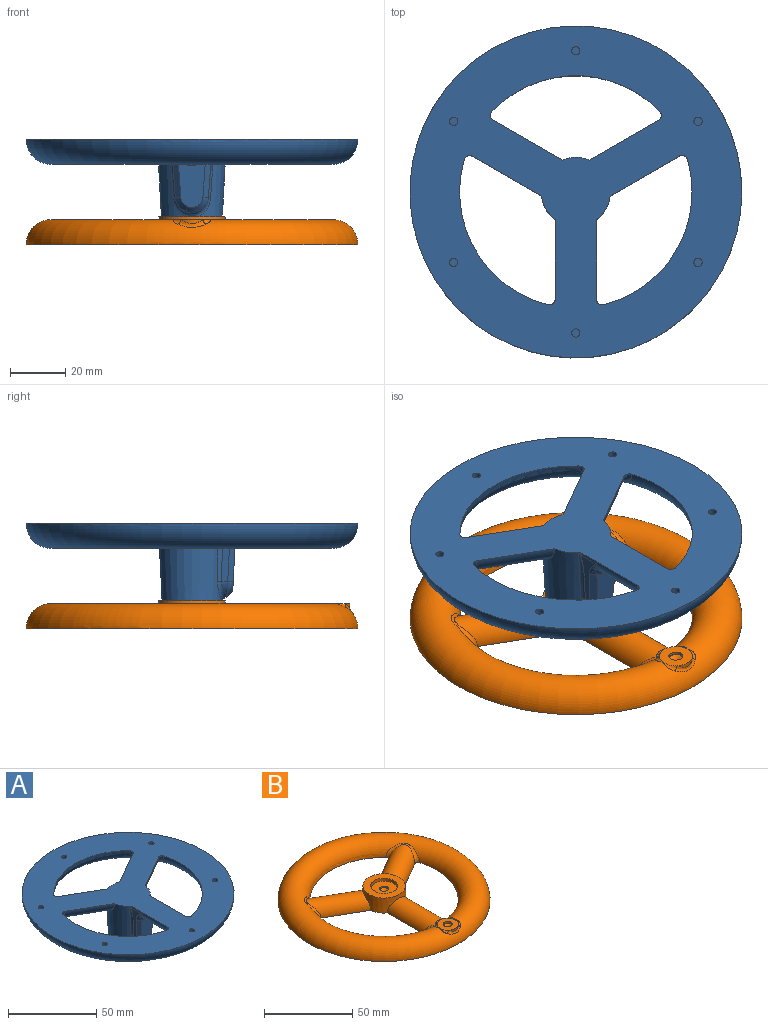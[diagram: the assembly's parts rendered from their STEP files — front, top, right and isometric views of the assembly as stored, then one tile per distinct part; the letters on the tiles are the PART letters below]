
ASSEMBLY  parts=2 mates=1
PART A: 42 faces, bbox 130.1x130.1x36.6 mm
  f0: plane 3x3mm, normal (0,0,1), area 7.1mm2, adj f1
  f1: cylinder r=1.5mm len=5mm, axis (0,0,-1), area 47.1mm2, adj f0,f2
  f2: plane 120.1x120.1mm, normal (0,0,1), area 7578.2mm2, adj f1,f4,f6,f8,f10,f12,f32,f33
  f3: plane 3x3mm, normal (0,0,1), area 7.1mm2, adj f4
  f4: cylinder r=1.5mm len=5mm, axis (0,0,-1), area 47.1mm2, adj f2,f3
  f5: plane 3x3mm, normal (0,0,1), area 7.1mm2, adj f6
  f6: cylinder r=1.5mm len=5mm, axis (0,0,-1), area 47.1mm2, adj f2,f5
  f7: plane 3x3mm, normal (0,0,1), area 7.1mm2, adj f8
  f8: cylinder r=1.5mm len=5mm, axis (0,0,-1), area 47.1mm2, adj f2,f7
  f9: plane 3x3mm, normal (0,0,1), area 7.1mm2, adj f10
  f10: cylinder r=1.5mm len=5mm, axis (0,0,-1), area 47.1mm2, adj f2,f9
  f11: plane 3x3mm, normal (0,0,1), area 7.1mm2, adj f12
  f12: cylinder r=1.5mm len=5mm, axis (0,0,-1), area 47.1mm2, adj f2,f11
  f13: bspline ~7.51x5.63mm, area 15.8mm2, adj f16,f17,f19,f20
  f14: bspline ~5.21x4.56mm, area 15.8mm2, adj f16,f18,f20,f21
  f15: cone r=0mm half-angle=59deg, axis (0,0,-1), area 22.9mm2, adj f22
  f16: plane 16.69x9.85mm, normal (0,-1,-0.05), area 128.1mm2, adj f13,f14,f17,f18,f20,f24
  f17: plane 12.89x2.93mm, normal (-0.7,-0.7,-0.09), area 36.6mm2, adj f13,f16,f25,f26
  f18: plane 12.89x2.93mm, normal (0.7,-0.7,-0.09), area 36.6mm2, adj f14,f16,f23,f27
  f19: cylinder r=6mm len=5.17mm, axis (0,1,0), area 7.3mm2, adj f13,f26,f29
  f20: bspline ~4.29x2.17mm, area 9.8mm2, adj f13,f14,f16,f29
  f21: cylinder r=6mm len=5.17mm, axis (0,1,0), area 7.3mm2, adj f14,f27,f29
  f22: cylinder r=2.5mm len=5mm, axis (0,0,-1), area 15.7mm2, adj f15,f31
  f23: bspline ~7.06x4.35mm, area 13.1mm2, adj f18,f24,f27,f41
  f24: bspline ~18.77x8.24mm, area 48.4mm2, adj f16,f23,f25,f41
  f25: bspline ~7.06x4.35mm, area 13.1mm2, adj f17,f24,f26,f41
  f26: plane 20.08x7.79mm, normal (-1,0,-0.07), area 62.3mm2, adj f17,f19,f25,f28,f33,f41
  f27: plane 20.08x7.79mm, normal (1,0,-0.07), area 62.3mm2, adj f18,f21,f23,f30,f32,f41
  f28: bspline ~21x2.21mm, area 30.7mm2, adj f26,f29,f33,f34
  f29: bspline ~13.63x9.03mm, area 48.7mm2, adj f19,f20,f21,f28,f30,f34
  f30: bspline ~21x2.21mm, area 30.7mm2, adj f27,f29,f32,f34
  f31: plane 21.86x21.86mm, normal (0,0,-1), area 355.5mm2, adj f22,f34
  f32: cone r=12.5mm half-angle=3deg, axis (0,0,-1), area 1.2mm2, adj f2,f27,f30,f41
  f33: cone r=12.5mm half-angle=3deg, axis (0,0,-1), area 3.6mm2, adj f2,f26,f28,f41
  f34: cone r=12.5mm half-angle=3deg, axis (0,0,1), area 1603.5mm2, adj f2,f28,f29,f30,f31,f39,f40
  f35: bspline ~17.28x11.32mm, area 65.2mm2, adj f2,f38,f40
  f36: bspline ~17.28x11.32mm, area 65.2mm2, adj f2,f38,f39
  f37: bspline ~19.97x8.68mm, area 65.2mm2, adj f2,f38,f41
  f38: torus R=51mm, axis (0,0,1), area 8643.7mm2, adj f2,f35,f36,f37
  f39: cylinder r=7.5mm len=38.21mm, axis (-0.87,-0.5,0), area 745.3mm2, adj f2,f34,f36
  f40: cylinder r=7.5mm len=32.49mm, axis (0.87,-0.5,0), area 679.9mm2, adj f2,f34,f35
  f41: cylinder r=7.5mm len=35.46mm, axis (0,1,0), area 588.8mm2, adj f2,f23,f24,f25,f26,f27,f32,f33
PART B: 45 faces, bbox 130x130x16.5 mm
  f0: bspline ~8.05x7.66mm, area 27.6mm2, adj f1,f5,f14,f32
  f1: cylinder r=7.5mm len=34.05mm, axis (0,1,0), area 718.7mm2, adj f0,f6,f15,f17,f19,f20,f32
  f2: cylinder r=6mm len=1.15mm, axis (0,0,-1), area 0.2mm2, adj f9,f12,f17
  f3: cylinder r=7.5mm len=38.23mm, axis (0.87,-0.5,0), area 728.8mm2, adj f6,f24,f32
  f4: cylinder r=7.5mm len=38.23mm, axis (-0.87,-0.5,0), area 728.2mm2, adj f6,f25,f32
  f5: torus R=51mm, axis (0,0,1), area 8497.3mm2, adj f0,f11,f12,f13,f15,f16,f21,f22
  f6: cone r=12.5mm half-angle=3deg, axis (0,0,-1), area 490.2mm2, adj f1,f3,f4,f7,f32
  f7: plane 23.95x23.95mm, normal (0,0,1), area 273.9mm2, adj f6,f26
  f8: cylinder r=6mm len=1.15mm, axis (0,0,-1), area 0.2mm2, adj f9,f16,f20
  f9: plane 12.04x12.04mm, normal (0,0,1), area 93.5mm2, adj f2,f8,f10,f11,f13,f19,f21,f23
  f10: cylinder r=6mm len=7.78mm, axis (0,0,-1), area 7.8mm2, adj f9,f22
  f11: bspline ~5.19x3.19mm, area 6.7mm2, adj f5,f9,f12
  f12: bspline ~2.95x2.6mm, area 1.5mm2, adj f2,f5,f11,f14
  f13: bspline ~5.19x3.19mm, area 6.7mm2, adj f5,f9,f16
  f14: sphere r=2mm, area 2.1mm2, adj f0,f12,f17
  f15: bspline ~7.89x7.23mm, area 27.6mm2, adj f1,f5,f18,f32
  f16: bspline ~2.95x2.6mm, area 1.5mm2, adj f5,f8,f13,f18
  f17: bspline ~3.05x2.9mm, area 2.2mm2, adj f1,f2,f14,f19
  f18: sphere r=2mm, area 2.1mm2, adj f15,f16,f20
  f19: bspline ~5.89x2.75mm, area 12.4mm2, adj f1,f9,f17,f20
  f20: bspline ~2.57x2.5mm, area 2.2mm2, adj f1,f8,f18,f19
  f21: bspline ~5.86x3.51mm, area 6.7mm2, adj f5,f9,f22
  f22: bspline ~11.01x3.2mm, area 17.5mm2, adj f5,f10,f21,f23
  f23: bspline ~5.86x3.51mm, area 6.7mm2, adj f5,f9,f22
  f24: bspline ~17.29x11.33mm, area 65.2mm2, adj f3,f5,f32
  f25: bspline ~17.29x11.33mm, area 65.2mm2, adj f4,f5,f32
  f26: cylinder r=7.5mm len=15mm, axis (0,0,1), area 94.2mm2, adj f7,f27
  f27: plane 15x15mm, normal (0,0,1), area 157.1mm2, adj f26,f31
  f28: cone r=0mm half-angle=59deg, axis (0,0,1), area 22.9mm2, adj f29
  f29: cylinder r=2.5mm len=5mm, axis (0,0,1), area 15.7mm2, adj f9,f28
  f30: cone r=0mm half-angle=59deg, axis (0,0,1), area 22.9mm2, adj f31
  f31: cylinder r=2.5mm len=5mm, axis (0,0,1), area 15.7mm2, adj f27,f30
  f32: plane 120.1x120.1mm, normal (0,0,-1), area 7578.2mm2, adj f0,f1,f3,f4,f5,f6,f15,f24
  f33: cylinder r=1.5mm len=5mm, axis (0,0,-1), area 47.1mm2, adj f32,f34
  f34: plane 3x3mm, normal (0,0,-1), area 7.1mm2, adj f33
  f35: cylinder r=1.5mm len=5mm, axis (0,0,-1), area 47.1mm2, adj f32,f36
  f36: plane 3x3mm, normal (0,0,-1), area 7.1mm2, adj f35
  f37: cylinder r=1.5mm len=5mm, axis (0,0,-1), area 47.1mm2, adj f32,f38
  f38: plane 3x3mm, normal (0,0,-1), area 7.1mm2, adj f37
  f39: cylinder r=1.5mm len=5mm, axis (0,0,-1), area 47.1mm2, adj f32,f40
  f40: plane 3x3mm, normal (0,0,-1), area 7.1mm2, adj f39
  f41: cylinder r=1.5mm len=5mm, axis (0,0,-1), area 47.1mm2, adj f32,f42
  f42: plane 3x3mm, normal (0,0,-1), area 7.1mm2, adj f41
  f43: cylinder r=1.5mm len=5mm, axis (0,0,-1), area 47.1mm2, adj f32,f44
  f44: plane 3x3mm, normal (0,0,-1), area 7.1mm2, adj f43
PLACE A t=(-34.36,0.73,-10.99)mm
PLACE B t=(-34.36,0.73,-48.99)mm
MATE revolute B.f26 <-> A.f32  axis (0,0,1) through (-34.36,0.73,-40.99)mm
